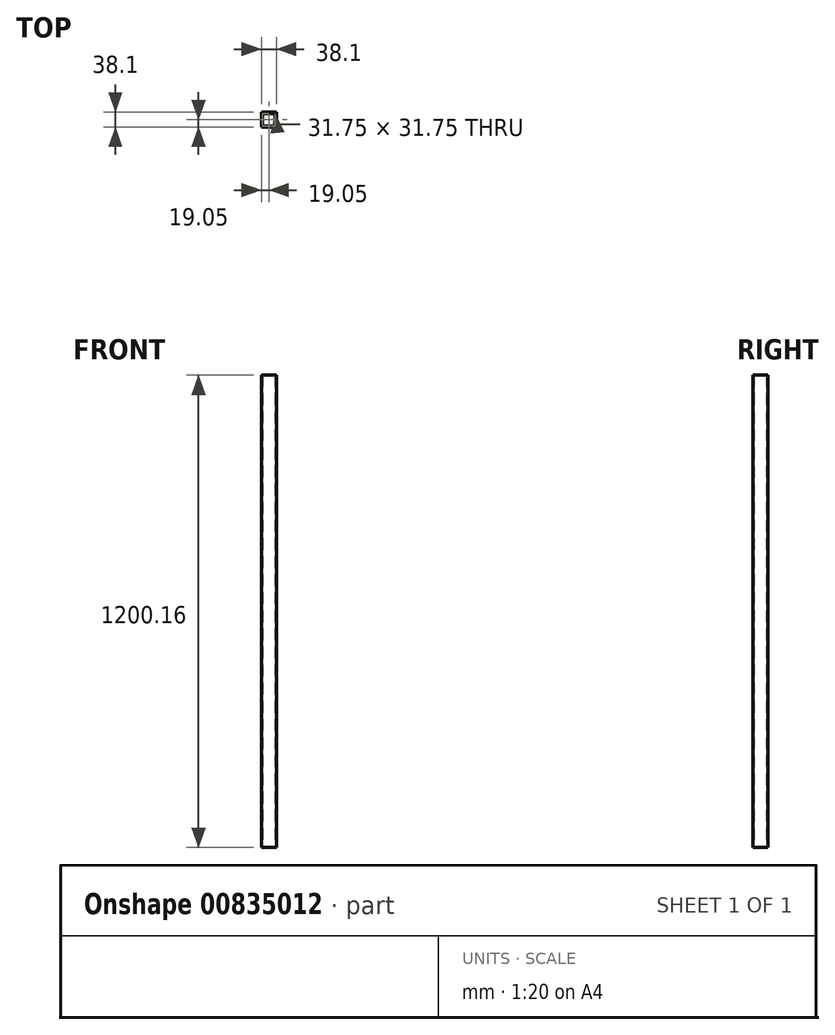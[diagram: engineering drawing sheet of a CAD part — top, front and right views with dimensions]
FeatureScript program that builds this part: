
annotation { "Feature Type Name" : "Feature", "Feature Type Description" : "" }
export const myFeature = defineFeature(function(context is Context, id is Id, definition is map)
    precondition{}
    {
        {
            var Q0;
            Q0=qCreatedBy(makeId("Top.planeOp"),FACE);
            var sketch = newSketch(context, id + "F0", { "sketchPlane" : qUnion([Q0])});
            skLineSegment(sketch, "E0.bottom", {"start": v(19.05, 19.05) * mm, "end": v(-19.05, 19.05) * mm});
            skLineSegment(sketch, "E0.top", {"start": v(19.05, -19.05) * mm, "end": v(-19.05, -19.05) * mm});
            skLineSegment(sketch, "E0.left", {"start": v(19.05, 19.05) * mm, "end": v(19.05, -19.05) * mm});
            skLineSegment(sketch, "E0.right", {"start": v(-19.05, 19.05) * mm, "end": v(-19.05, -19.05) * mm});
            skPoint(sketch, "E0.middle", {"position": v(0, 0) * mm});
            skLineSegment(sketch, "E1.bottom", {"start": v(15.88, 15.88) * mm, "end": v(-15.88, 15.88) * mm});
            skLineSegment(sketch, "E1.top", {"start": v(15.88, -15.88) * mm, "end": v(-15.88, -15.88) * mm});
            skLineSegment(sketch, "E1.left", {"start": v(15.88, 15.88) * mm, "end": v(15.88, -15.88) * mm});
            skLineSegment(sketch, "E1.right", {"start": v(-15.88, 15.88) * mm, "end": v(-15.88, -15.88) * mm});
            skSolve(sketch);
        }
        {
            var Q0;
            Q0 = qSketchRegion(id + "F0", true);
            extrude(context, id + "F1", {"entities" : qUnion([Q0]), "endBound" : BoundingType.SYMMETRIC, "depth" : 1200.15 * mm, "offsetDistance" : 25.4 * mm});
        }
    });
